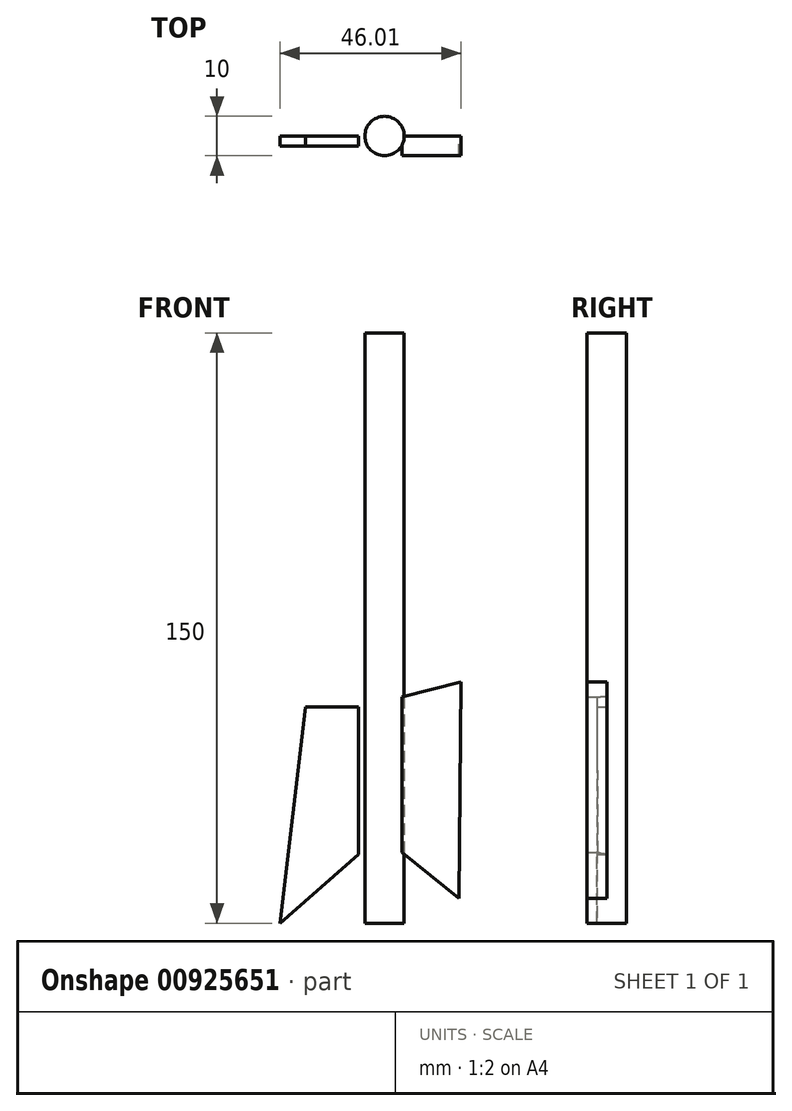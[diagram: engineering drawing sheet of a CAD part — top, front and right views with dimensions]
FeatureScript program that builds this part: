
annotation { "Feature Type Name" : "Feature", "Feature Type Description" : "" }
export const myFeature = defineFeature(function(context is Context, id is Id, definition is map)
    precondition{}
    {
        {
            var Q0;
            Q0=qCreatedBy(makeId("Top.planeOp"),FACE);
            var sketch = newSketch(context, id + "F0", { "sketchPlane" : qUnion([Q0])});
            skCircle(sketch, "E0", {"center": v(0, 0) * mm, "radius": 5 * mm});
            skSolve(sketch);
        }
        {
            var Q0;
            Q0=makeQuery(id+"F0.imprint","IMPRINT",FACE,{"disambiguationData":[TD([[makeQuery(id+"F0.imprint","IMPRINT",EDGE,{"derivedFrom":sQuery(id+"F0.wireOp",EDGE,"E0")}),1.0]])]});
            extrude(context, id + "F1", {"entities" : qUnion([Q0]), "depth" : 150 * mm, "offsetDistance" : 25 * mm});
        }
        {
            var Q0;
            Q0=qCreatedBy(makeId("Front.planeOp"),FACE);
            var sketch = newSketch(context, id + "F2", { "sketchPlane" : qUnion([Q0])});
            skLineSegment(sketch, "E1", {"start": v(-6.57, 55) * mm, "end": v(-20.07, 55) * mm});
            skLineSegment(sketch, "E2", {"start": v(-20.07, 55) * mm, "end": v(-26.57, 0) * mm});
            skLineSegment(sketch, "E3", {"start": v(-26.57, 0) * mm, "end": v(-6.57, 17.54) * mm});
            skLineSegment(sketch, "E4", {"start": v(-6.57, 55) * mm, "end": v(-6.57, 17.54) * mm});
            skSolve(sketch);
        }
        {
            var Q0;
            Q0=makeQuery(id+"F2.imprint","IMPRINT",FACE,{"disambiguationData":[TD([[makeQuery(id+"F2.imprint","IMPRINT",EDGE,{"derivedFrom":sQuery(id+"F2.wireOp",EDGE,"E1")}),1.0]])]});
            extrude(context, id + "F3", {"entities" : qUnion([Q0]), "depth" : 2.5 * mm, "offsetDistance" : 25 * mm});
        }
        {
            var Q0;
            Q0=qCreatedBy(makeId("Front.planeOp"),FACE);
            var sketch = newSketch(context, id + "F4", { "sketchPlane" : qUnion([Q0])});
            skLineSegment(sketch, "E5", {"start": v(4.44, 57.47) * mm, "end": v(19.44, 61.26) * mm});
            skLineSegment(sketch, "E6", {"start": v(19.44, 61.26) * mm, "end": v(18.95, 6.26) * mm});
            skLineSegment(sketch, "E7", {"start": v(18.95, 6.26) * mm, "end": v(4.45, 17.96) * mm});
            skLineSegment(sketch, "E8", {"start": v(4.45, 17.96) * mm, "end": v(4.44, 57.47) * mm});
            skSolve(sketch);
        }
        {
            var Q0;
            Q0=makeQuery(id+"F4.imprint","IMPRINT",FACE,{"disambiguationData":[TD([[makeQuery(id+"F4.imprint","IMPRINT",EDGE,{"derivedFrom":sQuery(id+"F4.wireOp",EDGE,"E5")}),-1.0]])]});
            extrude(context, id + "F5", {"entities" : qUnion([Q0]), "operationType" : NewBodyOperationType.ADD, "depth" : 5 * mm, "offsetDistance" : 25 * mm});
        }
    });
